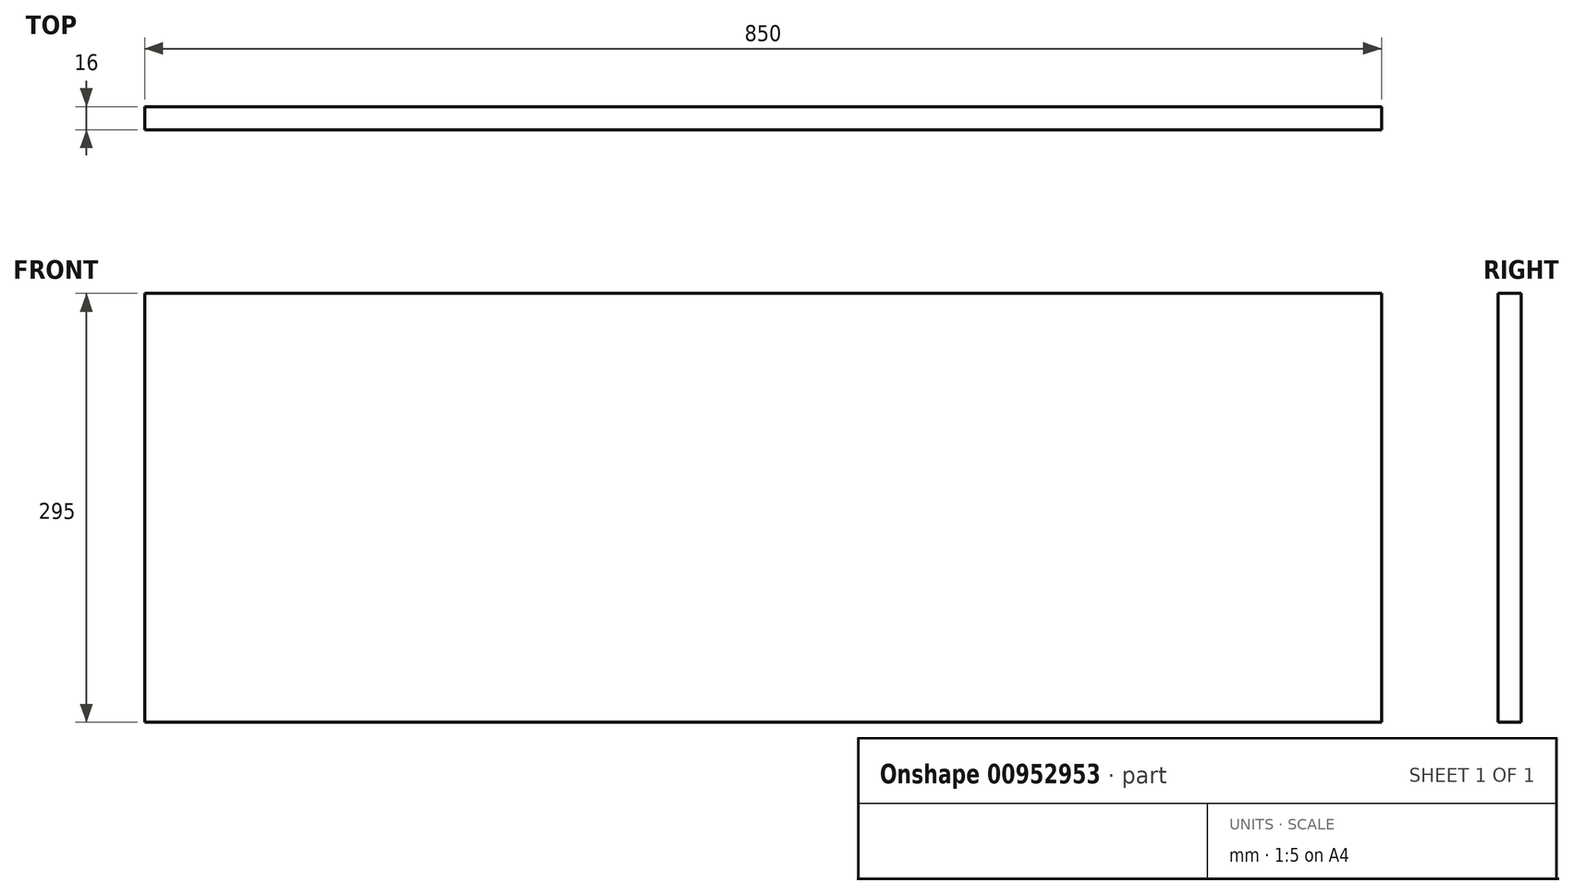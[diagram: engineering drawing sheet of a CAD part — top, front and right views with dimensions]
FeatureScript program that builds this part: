
annotation { "Feature Type Name" : "Feature", "Feature Type Description" : "" }
export const myFeature = defineFeature(function(context is Context, id is Id, definition is map)
    precondition{}
    {
        {
            var Q0;
            Q0=qCreatedBy(makeId("Front.planeOp"),FACE);
            var sketch = newSketch(context, id + "F0", { "sketchPlane" : qUnion([Q0])});
            skLineSegment(sketch, "E0.bottom", {"start": v(-420.85, 49.17) * mm, "end": v(429.15, 49.17) * mm});
            skLineSegment(sketch, "E0.top", {"start": v(-420.85, -245.83) * mm, "end": v(429.15, -245.83) * mm});
            skLineSegment(sketch, "E0.left", {"start": v(-420.85, 49.17) * mm, "end": v(-420.85, -245.83) * mm});
            skLineSegment(sketch, "E0.right", {"start": v(429.15, 49.17) * mm, "end": v(429.15, -245.83) * mm});
            skSolve(sketch);
        }
        {
            var Q0;
            Q0=makeQuery(id+"F0.imprint","IMPRINT",FACE,{"disambiguationData":[TD([[makeQuery(id+"F0.imprint","IMPRINT",EDGE,{"derivedFrom":sQuery(id+"F0.wireOp",EDGE,"E0.bottom")}),-1.0]])]});
            extrude(context, id + "F1", {"entities" : qUnion([Q0]), "depth" : 16 * mm, "offsetDistance" : 25 * mm});
        }
    });
